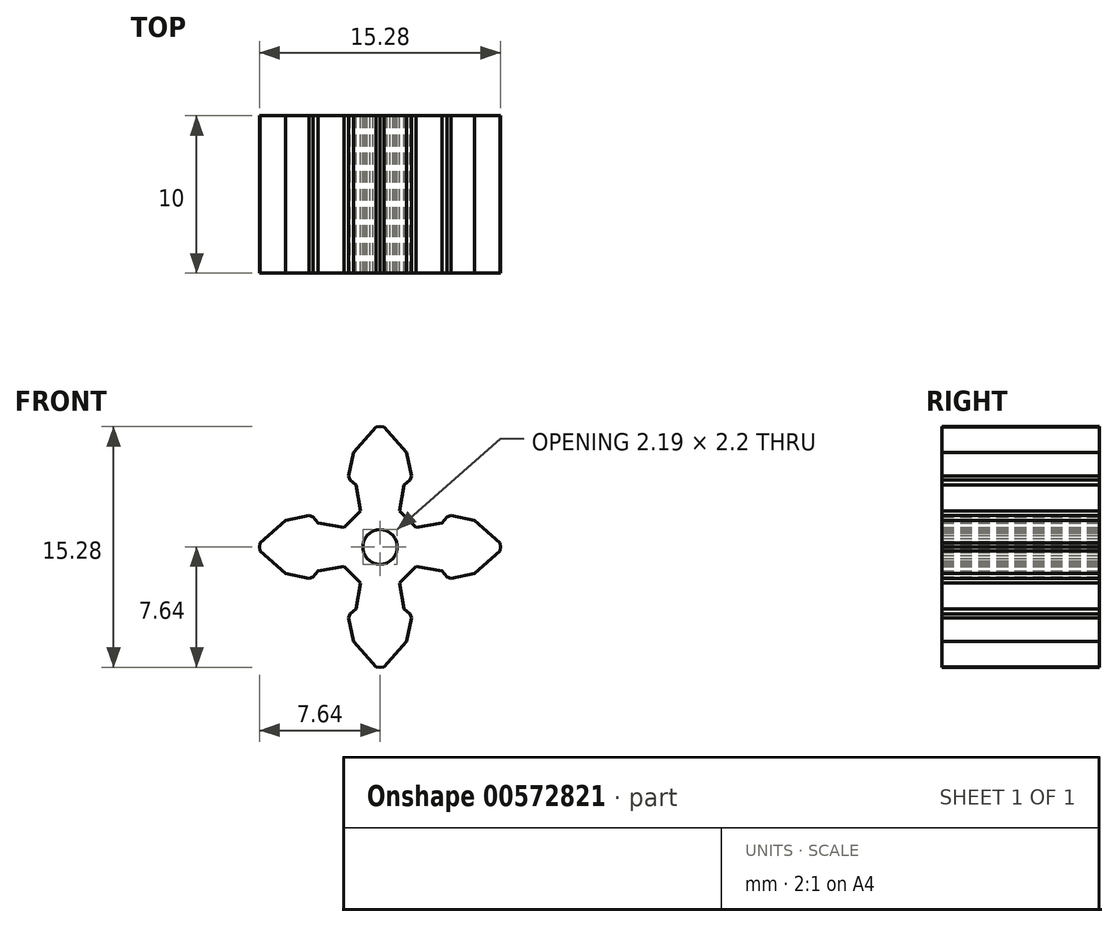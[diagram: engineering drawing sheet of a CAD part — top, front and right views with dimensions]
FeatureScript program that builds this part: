
annotation { "Feature Type Name" : "Feature", "Feature Type Description" : "" }
export const myFeature = defineFeature(function(context is Context, id is Id, definition is map)
    precondition{}
    {
        {
            var Q0;
            Q0=qCreatedBy(makeId("Front.planeOp"),FACE);
            var sketch = newSketch(context, id + "F0", { "sketchPlane" : qUnion([Q0])});
            skLineSegment(sketch, "E0", {"start": v(-0.24, -7.62) * mm, "end": v(0, -7.64) * mm});
            skLineSegment(sketch, "E1", {"start": v(0, -7.64) * mm, "end": v(0.24, -7.62) * mm});
            skLineSegment(sketch, "E2", {"start": v(0.24, -7.62) * mm, "end": v(1.68, -6) * mm});
            skLineSegment(sketch, "E3", {"start": v(1.68, -6) * mm, "end": v(1.99, -4.5) * mm});
            skLineSegment(sketch, "E4", {"start": v(1.99, -4.5) * mm, "end": v(1.9, -4.26) * mm});
            skLineSegment(sketch, "E5", {"start": v(1.9, -4.26) * mm, "end": v(1.53, -3.93) * mm});
            skLineSegment(sketch, "E6", {"start": v(1.53, -3.93) * mm, "end": v(1.25, -2.28) * mm});
            skLineSegment(sketch, "E7", {"start": v(1.25, -2.28) * mm, "end": v(2.28, -1.25) * mm});
            skLineSegment(sketch, "E8", {"start": v(2.28, -1.25) * mm, "end": v(3.93, -1.53) * mm});
            skLineSegment(sketch, "E9", {"start": v(3.93, -1.53) * mm, "end": v(4.26, -1.9) * mm});
            skLineSegment(sketch, "E10", {"start": v(4.26, -1.9) * mm, "end": v(4.5, -1.99) * mm});
            skLineSegment(sketch, "E11", {"start": v(4.5, -1.99) * mm, "end": v(6, -1.68) * mm});
            skLineSegment(sketch, "E12", {"start": v(6, -1.68) * mm, "end": v(7.62, -0.24) * mm});
            skLineSegment(sketch, "E13", {"start": v(7.62, -0.24) * mm, "end": v(7.64, 0) * mm});
            skLineSegment(sketch, "E14", {"start": v(7.64, 0) * mm, "end": v(7.62, 0.24) * mm});
            skLineSegment(sketch, "E15", {"start": v(7.62, 0.24) * mm, "end": v(6, 1.68) * mm});
            skLineSegment(sketch, "E16", {"start": v(6, 1.68) * mm, "end": v(4.5, 1.99) * mm});
            skLineSegment(sketch, "E17", {"start": v(4.5, 1.99) * mm, "end": v(4.26, 1.9) * mm});
            skLineSegment(sketch, "E18", {"start": v(4.26, 1.9) * mm, "end": v(3.93, 1.53) * mm});
            skLineSegment(sketch, "E19", {"start": v(3.93, 1.53) * mm, "end": v(2.28, 1.25) * mm});
            skLineSegment(sketch, "E20", {"start": v(2.28, 1.25) * mm, "end": v(1.25, 2.28) * mm});
            skLineSegment(sketch, "E21", {"start": v(1.25, 2.28) * mm, "end": v(1.53, 3.93) * mm});
            skLineSegment(sketch, "E22", {"start": v(1.53, 3.93) * mm, "end": v(1.9, 4.26) * mm});
            skLineSegment(sketch, "E23", {"start": v(1.9, 4.26) * mm, "end": v(1.99, 4.5) * mm});
            skLineSegment(sketch, "E24", {"start": v(1.99, 4.5) * mm, "end": v(1.68, 6) * mm});
            skLineSegment(sketch, "E25", {"start": v(1.68, 6) * mm, "end": v(0.24, 7.62) * mm});
            skLineSegment(sketch, "E26", {"start": v(0.24, 7.62) * mm, "end": v(0, 7.64) * mm});
            skLineSegment(sketch, "E27", {"start": v(0, 7.64) * mm, "end": v(-0.24, 7.62) * mm});
            skLineSegment(sketch, "E28", {"start": v(-0.24, 7.62) * mm, "end": v(-1.68, 6) * mm});
            skLineSegment(sketch, "E29", {"start": v(-1.68, 6) * mm, "end": v(-1.99, 4.5) * mm});
            skLineSegment(sketch, "E30", {"start": v(-1.99, 4.5) * mm, "end": v(-1.9, 4.26) * mm});
            skLineSegment(sketch, "E31", {"start": v(-1.9, 4.26) * mm, "end": v(-1.53, 3.93) * mm});
            skLineSegment(sketch, "E32", {"start": v(-1.53, 3.93) * mm, "end": v(-1.25, 2.28) * mm});
            skLineSegment(sketch, "E33", {"start": v(-1.25, 2.28) * mm, "end": v(-2.28, 1.25) * mm});
            skLineSegment(sketch, "E34", {"start": v(-2.28, 1.25) * mm, "end": v(-3.93, 1.53) * mm});
            skLineSegment(sketch, "E35", {"start": v(-3.93, 1.53) * mm, "end": v(-4.26, 1.9) * mm});
            skLineSegment(sketch, "E36", {"start": v(-4.26, 1.9) * mm, "end": v(-4.5, 1.99) * mm});
            skLineSegment(sketch, "E37", {"start": v(-4.5, 1.99) * mm, "end": v(-6, 1.68) * mm});
            skLineSegment(sketch, "E38", {"start": v(-6, 1.68) * mm, "end": v(-7.62, 0.24) * mm});
            skLineSegment(sketch, "E39", {"start": v(-7.62, 0.24) * mm, "end": v(-7.64, 0) * mm});
            skLineSegment(sketch, "E40", {"start": v(-7.64, 0) * mm, "end": v(-7.62, -0.24) * mm});
            skLineSegment(sketch, "E41", {"start": v(-7.62, -0.24) * mm, "end": v(-6, -1.68) * mm});
            skLineSegment(sketch, "E42", {"start": v(-6, -1.68) * mm, "end": v(-4.5, -1.99) * mm});
            skLineSegment(sketch, "E43", {"start": v(-4.5, -1.99) * mm, "end": v(-4.26, -1.9) * mm});
            skLineSegment(sketch, "E44", {"start": v(-4.26, -1.9) * mm, "end": v(-3.93, -1.53) * mm});
            skLineSegment(sketch, "E45", {"start": v(-3.93, -1.53) * mm, "end": v(-2.28, -1.25) * mm});
            skLineSegment(sketch, "E46", {"start": v(-2.28, -1.25) * mm, "end": v(-1.25, -2.28) * mm});
            skLineSegment(sketch, "E47", {"start": v(-1.25, -2.28) * mm, "end": v(-1.53, -3.93) * mm});
            skLineSegment(sketch, "E48", {"start": v(-1.53, -3.93) * mm, "end": v(-1.9, -4.26) * mm});
            skLineSegment(sketch, "E49", {"start": v(-1.9, -4.26) * mm, "end": v(-1.99, -4.5) * mm});
            skLineSegment(sketch, "E50", {"start": v(-1.99, -4.5) * mm, "end": v(-1.68, -6) * mm});
            skLineSegment(sketch, "E51", {"start": v(-1.68, -6) * mm, "end": v(-0.24, -7.62) * mm});
            skLineSegment(sketch, "E52", {"start": v(0.23, -1.08) * mm, "end": v(0, -1.1) * mm});
            skLineSegment(sketch, "E53", {"start": v(0, -1.1) * mm, "end": v(-0.23, -1.08) * mm});
            skLineSegment(sketch, "E54", {"start": v(-0.23, -1.08) * mm, "end": v(-0.45, -1) * mm});
            skLineSegment(sketch, "E55", {"start": v(-0.45, -1) * mm, "end": v(-0.65, -0.89) * mm});
            skLineSegment(sketch, "E56", {"start": v(-0.65, -0.89) * mm, "end": v(-0.82, -0.74) * mm});
            skLineSegment(sketch, "E57", {"start": v(-0.82, -0.74) * mm, "end": v(-0.95, -0.55) * mm});
            skLineSegment(sketch, "E58", {"start": v(-0.95, -0.55) * mm, "end": v(-1.05, -0.34) * mm});
            skLineSegment(sketch, "E59", {"start": v(-1.05, -0.34) * mm, "end": v(-1.1, -0.11) * mm});
            skLineSegment(sketch, "E60", {"start": v(-1.1, -0.11) * mm, "end": v(-1.1, 0.11) * mm});
            skLineSegment(sketch, "E61", {"start": v(-1.1, 0.11) * mm, "end": v(-1.05, 0.34) * mm});
            skLineSegment(sketch, "E62", {"start": v(-1.05, 0.34) * mm, "end": v(-0.95, 0.55) * mm});
            skLineSegment(sketch, "E63", {"start": v(-0.95, 0.55) * mm, "end": v(-0.82, 0.74) * mm});
            skLineSegment(sketch, "E64", {"start": v(-0.82, 0.74) * mm, "end": v(-0.65, 0.89) * mm});
            skLineSegment(sketch, "E65", {"start": v(-0.65, 0.89) * mm, "end": v(-0.45, 1) * mm});
            skLineSegment(sketch, "E66", {"start": v(-0.45, 1) * mm, "end": v(-0.23, 1.08) * mm});
            skLineSegment(sketch, "E67", {"start": v(-0.23, 1.08) * mm, "end": v(0, 1.1) * mm});
            skLineSegment(sketch, "E68", {"start": v(0, 1.1) * mm, "end": v(0.23, 1.08) * mm});
            skLineSegment(sketch, "E69", {"start": v(0.23, 1.08) * mm, "end": v(0.45, 1) * mm});
            skLineSegment(sketch, "E70", {"start": v(0.45, 1) * mm, "end": v(0.65, 0.89) * mm});
            skLineSegment(sketch, "E71", {"start": v(0.65, 0.89) * mm, "end": v(0.82, 0.74) * mm});
            skLineSegment(sketch, "E72", {"start": v(0.82, 0.74) * mm, "end": v(0.95, 0.55) * mm});
            skLineSegment(sketch, "E73", {"start": v(0.95, 0.55) * mm, "end": v(1.05, 0.34) * mm});
            skLineSegment(sketch, "E74", {"start": v(1.05, 0.34) * mm, "end": v(1.1, 0.11) * mm});
            skLineSegment(sketch, "E75", {"start": v(1.1, 0.11) * mm, "end": v(1.1, -0.11) * mm});
            skLineSegment(sketch, "E76", {"start": v(1.1, -0.11) * mm, "end": v(1.05, -0.34) * mm});
            skLineSegment(sketch, "E77", {"start": v(1.05, -0.34) * mm, "end": v(0.95, -0.55) * mm});
            skLineSegment(sketch, "E78", {"start": v(0.95, -0.55) * mm, "end": v(0.82, -0.74) * mm});
            skLineSegment(sketch, "E79", {"start": v(0.82, -0.74) * mm, "end": v(0.65, -0.89) * mm});
            skLineSegment(sketch, "E80", {"start": v(0.65, -0.89) * mm, "end": v(0.45, -1) * mm});
            skLineSegment(sketch, "E81", {"start": v(0.45, -1) * mm, "end": v(0.23, -1.08) * mm});
            skSolve(sketch);
        }
        {
            var Q0;
            Q0 = qSketchRegion(id + "F0", true);
            extrude(context, id + "F1", {"entities" : qUnion([Q0]), "depth" : 10 * mm, "offsetDistance" : 25 * mm});
        }
    });
